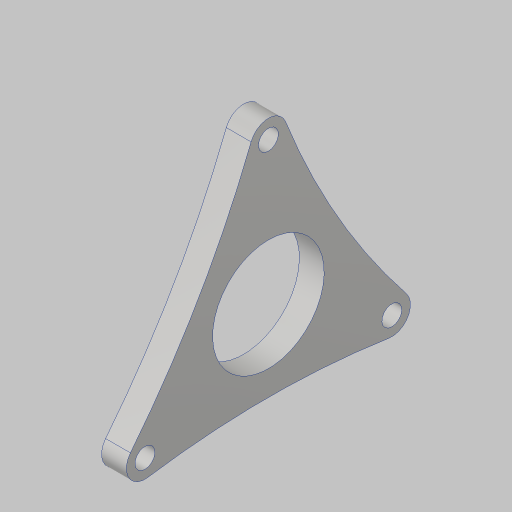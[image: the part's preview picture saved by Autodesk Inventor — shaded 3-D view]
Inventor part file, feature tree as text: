
AUTODESK INVENTOR PART (.ipt)
format: ipt  version: 2023.5 (Build 275446000, 446)  size: 118,272 bytes
history: native  units: in
note: dims shown in document units (in); Inventor stores cm internally (conversion verified against a paired STEP export)
features: sketch x1, extrude x1, hole x1
ambient origin geometry x8: Origin, YZ Plane, XZ Plane, XY Plane, X Axis, Y Axis, Z Axis, Center Point
bodies: Solid1 (feature_tree)
feature tree (3):
  sketch  "Sketch1"  dims[d0=2.5in d1=0.375in d2=1.1811in d4=360.0deg d6=1.125in d7=0.25in d8=0.25in d9=0.0in d10=0.201in d11=0.38in d12=0.385in d13=0.25in d14=0.5635in d15=1.0in d16=0.8108in]
  extrude  "Extrusion1"  Depth=0.25in
  hole  "Hole1"  [1 undecoded]
note: 1 required parameter value undecoded (feature->parameter linkage not recoverable at this tier; creation-order binding heuristic only, values carry confidence <= 0.55)
